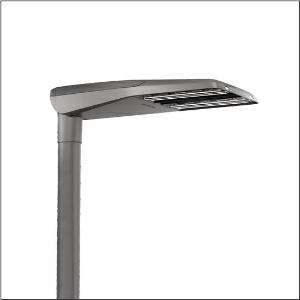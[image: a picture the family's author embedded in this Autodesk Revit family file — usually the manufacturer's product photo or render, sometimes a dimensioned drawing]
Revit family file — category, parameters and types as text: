
# Revit family: streetlight_sl_11_iq_midi___st1_2p1_0_5xc3g41e08me_f4ca
name_source: partatom
category: Lighting Fixtures
units: mm (PartAtom-declared; Revit-internal decimal feet)

## family parameters
Cut with Voids When Loaded = No
Host = Face
Light Source = No
Part Type = Normal
Room Calculation Point = No
Round Connector Dimension = Use Diameter
Shared = No

## types (1)
- --- (1 x LED, 18520 lm, 124.7 W, 4000K)
    Apparent Load = 125 VA
    CIE Flux Codes = 31 68 95 100 100
    Color Rendering = 70
    Color Temperature = 4000K
    Default Elevation = 1800 mm
    Description = Streetlight SL 11 iQ midi, mast luminaire, primary light control with 3 zone facetted reflector, of plastic, silver coated, highly specular, primary optical cover: cover, of PMMA, transparent, light distribution: ST1.2P1.0, light emission: direct distribution, primary light characteristic: asymmetric, installation type: post-top, side-entry, LED, High Power LED, rated luminous flux: 18.520lm, luminous efficacy: 149lm/W, light colour: 740, colour temperature: 4000K, control: optimised constant luminous flux control (CLO 2.0), Desk-Remote (wireless, voltage-free reading and setting of iQ features in the workshop via application-optimized NFC function/RFID function), Light-Fading, Smart-Wire, Night-Set, Lumen-Switch, Temp-Guard, Auto-Match, with cable H07RN-F 5x 1.5mm², mains connection: 230..240V, AC, 50/60Hz, connection cable pre-assembled, cable length: 12,5m, start of lifetime: 125W, end of service life: 132W, reduction: 57W, luminaire housing, of diecast aluminium, powder-coated, Siteco® metallic grey (DB 702S), please order mast flange separately, inclination adjustable without tools: 0°, 5°, 10°, 15° (post-top) | 0°, -5°, -10°, -15° (side-entry), sealing non-destructively replaceable, multi-level sealing system, length: 780mm, width: 376mm, height: 118mm, mast flange for spigot size: 42mm (side-entry): 5XC10008XM4, 60/48mm (side-entry/post-top): 5XC10108XM2, 76/60mm (side-entry/post-top): 5XC10108XM1, equipment: Power, protection rating (complete): IP66, insulation class (complete): insulation class II (safety insulation), certification: CE, ENEC, VDE, impact resistance: IK09, permissible operating ambient temperature for outdoor applications: -25..+50°C, standard-compliant lighting for roads and squares, Environmental Product Declaration (EPD) tested and certified by an independent institute, packaging unit: 1 piece

Light Distribution: ST1.2P1.0
    Height = 118 mm
    Lamp = 1 x LED
    Lamp Light Flux = 18520 lm
    Lamp Power = 124.7 W
    Lamp count = 1
    Length = 780 mm
    Luminous efficacy = 149 lm/W
    Manufacturer = Siteco
    ModVariant = No
    Model = 5XC3G41E08ME
    Number of Poles = 1
    OnlyDefault = Yes
    Power Factor = 1
    Product Name = Streetlight SL 11 iQ midi | ST1.2P1.0
    Product group = mast luminaire | pylon top
    ProductGroupID = 6100
    Protection Class = Protection class II
    Protection Degree = IP 66
    RLX_Detail_Level = 1
    RLX_Emergency_Light_Flux = 0 lm
    RLX_Emergency_Type = 0
    RLX_Emergency_Type_DB = No
    RlxData = <blob elided: 70633 chars, md5=18d1f61b>
    Socket = socket
    Standby Power = 0 W
    System Light Flux = 18520 lm
    System Power = 125 W
    Type Comments = factory setting: luminous flux: 100 % | dim-lin: 254 | 557 mA
    Type Image = l_1005960.jpg
    URL = http://relux.com
    VarID = @adj_129611
    Voltage = 0 V
    Weight = 0.00 kg
    Width = 376 mm

## geometry (parser evidence)
native form markers: Blend x4, Sweep x8
no freeform markers — native parametric forms only
